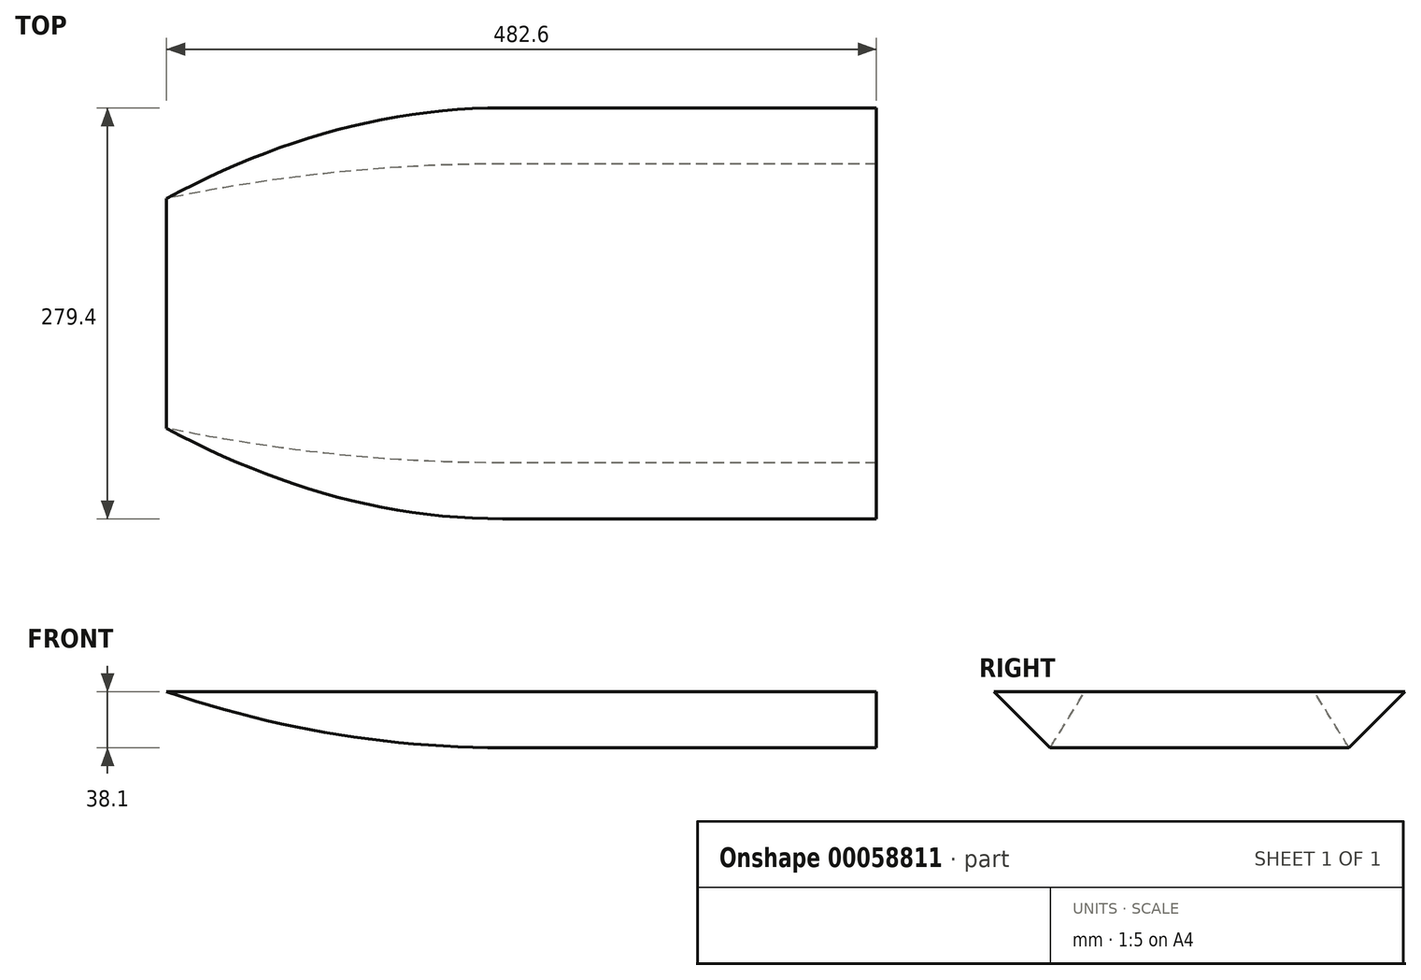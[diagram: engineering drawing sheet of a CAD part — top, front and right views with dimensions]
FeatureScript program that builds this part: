
annotation { "Feature Type Name" : "Feature", "Feature Type Description" : "" }
export const myFeature = defineFeature(function(context is Context, id is Id, definition is map)
    precondition{}
    {
        {
            var Q0;
            Q0=qCreatedBy(makeId("Front.planeOp"),FACE);
            var sketch = newSketch(context, id + "F0", { "sketchPlane" : qUnion([Q0])});
            skLineSegment(sketch, "E0.bottom", {"start": v(0, 0) * mm, "end": v(254, 0) * mm});
            skLineSegment(sketch, "E0.right", {"start": v(254, 0) * mm, "end": v(254, 38.1) * mm});
            skLineSegment(sketch, "E1", {"start": v(254, 38.1) * mm, "end": v(-228.6, 38.1) * mm});
            skArc(sketch, "E2", {"start": v(0, 0) * mm, "mid": v(-115.88, 9.6) * mm, "end": v(-228.6, 38.1) * mm});
            skSolve(sketch);
        }
        {
            var Q0;
            Q0=makeQuery(id+"F0.imprint","IMPRINT",FACE,{"disambiguationData":[TD([[makeQuery(id+"F0.imprint","IMPRINT",EDGE,{"derivedFrom":sQuery(id+"F0.wireOp",EDGE,"E0.bottom")}),1.0]])]});
            extrude(context, id + "F1", {"entities" : qUnion([Q0]), "depth" : 88.9 * mm});
        }
        {
            var Q0;
            Q0=makeQuery(id+"F1.opExtrude","CAP_FACE",FACE,{"disambiguationData":[OSD([sQuery(id+"F0.wireOp",EDGE,"E0.bottom"),sQuery(id+"F0.wireOp",EDGE,"E0.right"),sQuery(id+"F0.wireOp",EDGE,"E1"),sQuery(id+"F0.wireOp",EDGE,"E2")])],"isStart":false});
            extrude(context, id + "F2", {"entities" : qUnion([Q0]), "operationType" : NewBodyOperationType.ADD, "depth" : 50.8 * mm});
        }
        {
            var Q0;
            {var subQ0=sQuery(id+"F0.wireOp",EDGE,"E1");Q0=makeQuery(id+"F2.boolean.opBoolean","MERGE",FACE,{"derivedFrom":[makeQuery(id+"F1.opExtrude","SWEPT_FACE",FACE,{"disambiguationData":[OSD([subQ0])]}),makeQuery(id+"F2.opExtrude","SWEPT_FACE",FACE,{"disambiguationData":[OSD([subQ0])]})]});}
            var sketch = newSketch(context, id + "F3", { "sketchPlane" : qUnion([Q0])});
            skLineSegment(sketch, "E3", {"start": v(-304.42, -139.7) * mm, "end": v(0, -139.7) * mm});
            skArc(sketch, "E4", {"start": v(-228.6, -114.3) * mm, "mid": v(-115, -133.33) * mm, "end": v(0, -139.7) * mm});
            skLineSegment(sketch, "E5", {"start": v(-304.42, -139.7) * mm, "end": v(-304.42, -114.3) * mm});
            skLineSegment(sketch, "E6", {"start": v(-304.42, -114.3) * mm, "end": v(-228.6, -114.3) * mm});
            skSolve(sketch);
        }
        {
            var Q0;
            Q0 = qSketchRegion(id + "F3", true);
            extrude(context, id + "F4", {"entities" : qUnion([Q0]), "operationType" : NewBodyOperationType.REMOVE, "endBound" : BoundingType.THROUGH_ALL, "oppositeDirection" : true, "depth" : 25.4 * mm});
        }
        {
            var Q0;
            Q0=makeQuery(id+"F2.opExtrude","CAP_EDGE",EDGE,{"disambiguationData":[OSD([sQuery(id+"F0.wireOp",EDGE,"E0.bottom")])],"isStart":false});
            chamfer(context, id + "F5", {"entities" : qUnion([Q0]), "width" : 38.1 * mm, "tangentPropagation" : true});
        }
        {
            var Q0;
            Q0=makeQuery(id+"F1.opExtrude","SWEPT_BODY",BODY,{"disambiguationData":[OSD([sQuery(id+"F0.wireOp",EDGE,"E0.bottom"),sQuery(id+"F0.wireOp",EDGE,"E0.right"),sQuery(id+"F0.wireOp",EDGE,"E1"),sQuery(id+"F0.wireOp",EDGE,"E2")])]});
            var Q1;
            Q1=qCreatedBy(makeId("Front.planeOp"),FACE);
            mirror(context, id + "F6", {"operationType" : NewBodyOperationType.ADD, "entities" : qUnion([Q0]), "mirrorPlane" : qUnion([Q1])});
        }
    });
